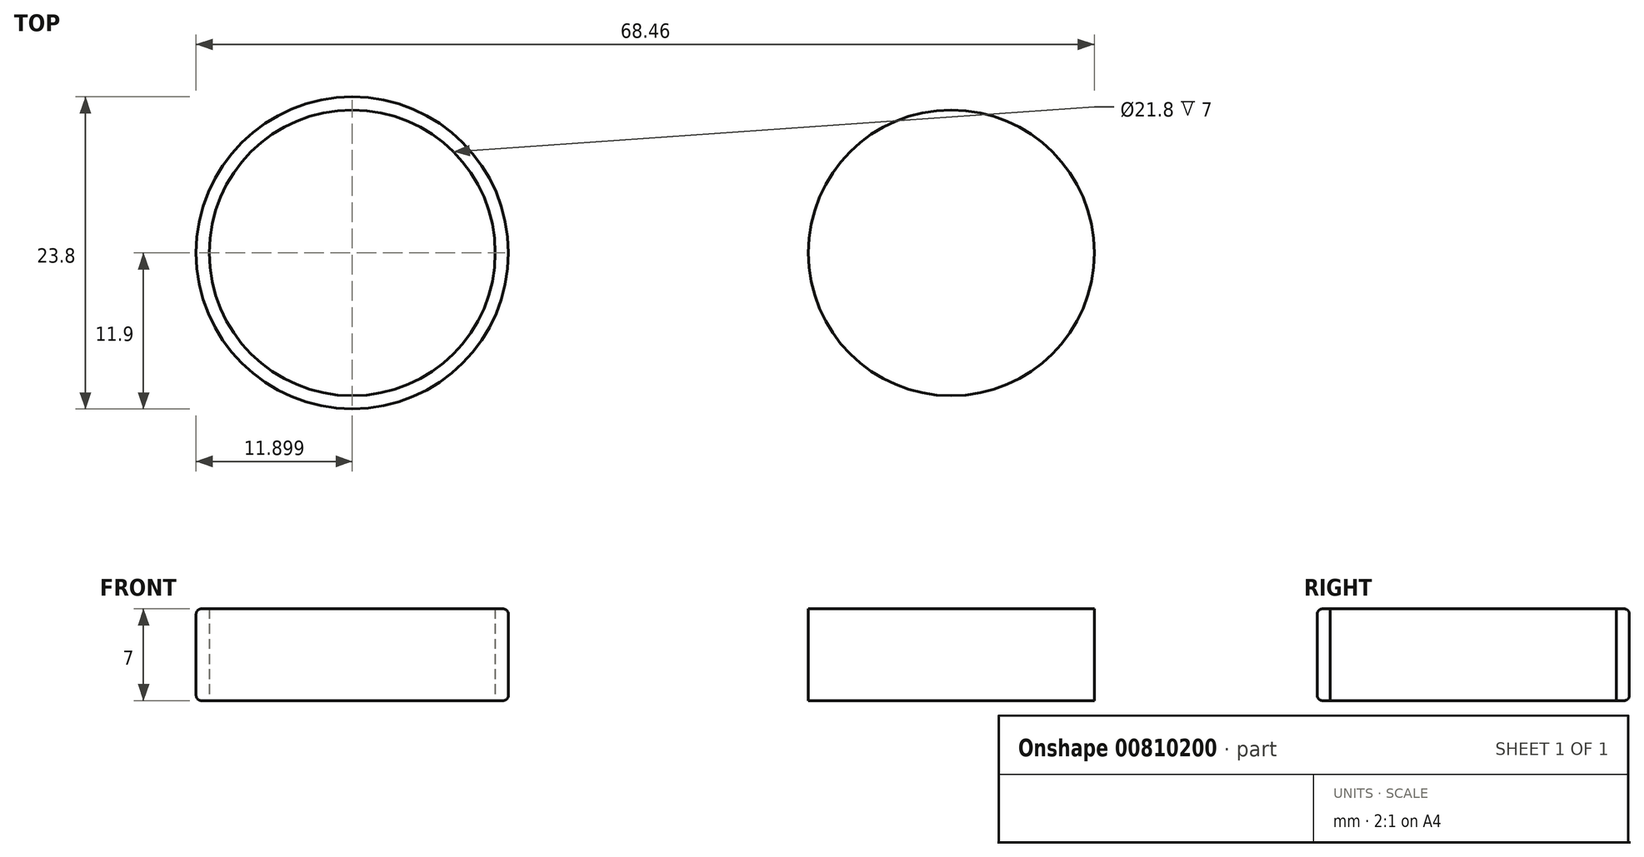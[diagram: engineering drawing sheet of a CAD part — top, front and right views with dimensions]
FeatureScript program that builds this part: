
annotation { "Feature Type Name" : "Feature", "Feature Type Description" : "" }
export const myFeature = defineFeature(function(context is Context, id is Id, definition is map)
    precondition{}
    {
        {
            var Q0;
            Q0=qCreatedBy(makeId("Top.planeOp"),FACE);
            var sketch = newSketch(context, id + "F0", { "sketchPlane" : qUnion([Q0])});
            skCircle(sketch, "E0", {"center": v(0, 0) * mm, "radius": 10.9 * mm});
            skCircle(sketch, "E1", {"center": v(0, 0) * mm, "radius": 11.9 * mm});
            skCircle(sketch, "E2", {"center": v(-22.83, 0) * mm, "radius": 10.9 * mm});
            skCircle(sketch, "E3", {"center": v(-22.83, 0) * mm, "radius": 11.9 * mm});
            skCircle(sketch, "E4.MirrorC", {"center": v(22.83, 0) * mm, "radius": 10.9 * mm});
            skCircle(sketch, "E5.MirrorC", {"center": v(22.83, 0) * mm, "radius": 11.9 * mm});
            skSolve(sketch);
        }
        {
            var Q0;
            {var subQ0=sQuery(id+"F0.wireOp",EDGE,"E1");var subQ1=sQuery(id+"F0.wireOp",EDGE,"E3");var subQ2=makeQuery(id+"F0.imprint","INTERSECT",VERTEX,{"disambiguationData":[OD(0.0)],"derivedFrom":[subQ1,subQ0]});Q0=makeQuery(id+"F0.imprint","IMPRINT",FACE,{"disambiguationData":[TD([[makeQuery(id+"F0.imprint","IMPRINT",EDGE,{"disambiguationData":[TD([[subQ2,1.0]])],"derivedFrom":subQ1}),1.0]])]});}
            var Q1;
            Q1=makeQuery(id+"F0.imprint","IMPRINT",FACE,{"disambiguationData":[TD([[makeQuery(id+"F0.imprint","IMPRINT",EDGE,{"derivedFrom":sQuery(id+"F0.wireOp",EDGE,"E0")}),1.0]])]});
            var Q2;
            Q2=makeQuery(id+"F0.imprint","IMPRINT",FACE,{"disambiguationData":[TD([[makeQuery(id+"F0.imprint","IMPRINT",EDGE,{"derivedFrom":sQuery(id+"F0.wireOp",EDGE,"E2")}),-1.0]])]});
            var Q3;
            {var subQ0=sQuery(id+"F0.wireOp",EDGE,"E5.MirrorC");var subQ1=sQuery(id+"F0.wireOp",EDGE,"E1");var subQ2=makeQuery(id+"F0.imprint","INTERSECT",VERTEX,{"disambiguationData":[OD(0.0)],"derivedFrom":[subQ1,subQ0]});Q3=makeQuery(id+"F0.imprint","IMPRINT",FACE,{"disambiguationData":[TD([[makeQuery(id+"F0.imprint","IMPRINT",EDGE,{"disambiguationData":[TD([[subQ2,-1.0]])],"derivedFrom":subQ1}),-1.0]])]});}
            var Q4;
            Q4=makeQuery(id+"F0.imprint","IMPRINT",FACE,{"disambiguationData":[TD([[makeQuery(id+"F0.imprint","IMPRINT",EDGE,{"derivedFrom":sQuery(id+"F0.wireOp",EDGE,"E4.MirrorC")}),1.0]])]});
            extrude(context, id + "F1", {"entities" : qUnion([Q0, Q1, Q2, Q3, Q4]), "depth" : 7 * mm, "offsetDistance" : 25 * mm});
        }
        {
            var Q0;
            Q0=makeQuery(id+"F1.opExtrude","CAP_EDGE",EDGE,{"disambiguationData":[OSD([sQuery(id+"F0.wireOp",EDGE,"E3")])],"isStart":false});
            var Q1;
            Q1=makeQuery(id+"F1.opExtrude","CAP_EDGE",EDGE,{"disambiguationData":[OSD([sQuery(id+"F0.wireOp",EDGE,"E5.MirrorC")])],"isStart":false});
            var Q2;
            Q2=makeQuery(id+"F1.opExtrude","CAP_EDGE",EDGE,{"disambiguationData":[OSD([sQuery(id+"F0.wireOp",EDGE,"E5.MirrorC")])],"isStart":true});
            var Q3;
            Q3=makeQuery(id+"F1.opExtrude","CAP_EDGE",EDGE,{"disambiguationData":[OSD([sQuery(id+"F0.wireOp",EDGE,"E3")])],"isStart":true});
            var Q4;
            {var subQ0=sQuery(id+"F0.wireOp",EDGE,"E1");Q4=makeQuery(id+"F1.opExtrude","CAP_EDGE",EDGE,{"disambiguationData":[OSD([subQ0]),TDD([makeQuery(id+"F0.imprint","IMPRINT",EDGE,{"disambiguationData":[TD([[makeQuery(id+"F0.imprint","INTERSECT",VERTEX,{"disambiguationData":[OD(1.0)],"derivedFrom":[sQuery(id+"F0.wireOp",EDGE,"E3"),subQ0]}),1.0]])],"derivedFrom":subQ0})])],"isStart":true});}
            var Q5;
            {var subQ0=sQuery(id+"F0.wireOp",EDGE,"E1");Q5=makeQuery(id+"F1.opExtrude","CAP_EDGE",EDGE,{"disambiguationData":[OSD([subQ0]),TDD([makeQuery(id+"F0.imprint","IMPRINT",EDGE,{"disambiguationData":[TD([[makeQuery(id+"F0.imprint","INTERSECT",VERTEX,{"disambiguationData":[OD(1.0)],"derivedFrom":[sQuery(id+"F0.wireOp",EDGE,"E3"),subQ0]}),1.0]])],"derivedFrom":subQ0})])],"isStart":false});}
            var Q6;
            {var subQ0=sQuery(id+"F0.wireOp",EDGE,"E1");Q6=makeQuery(id+"F1.opExtrude","CAP_EDGE",EDGE,{"disambiguationData":[OSD([subQ0]),TDD([makeQuery(id+"F0.imprint","IMPRINT",EDGE,{"disambiguationData":[TD([[makeQuery(id+"F0.imprint","INTERSECT",VERTEX,{"disambiguationData":[OD(0.0)],"derivedFrom":[sQuery(id+"F0.wireOp",EDGE,"E3"),subQ0]}),-1.0]])],"derivedFrom":subQ0})])],"isStart":false});}
            var Q7;
            {var subQ0=sQuery(id+"F0.wireOp",EDGE,"E1");Q7=makeQuery(id+"F1.opExtrude","CAP_EDGE",EDGE,{"disambiguationData":[OSD([subQ0]),TDD([makeQuery(id+"F0.imprint","IMPRINT",EDGE,{"disambiguationData":[TD([[makeQuery(id+"F0.imprint","INTERSECT",VERTEX,{"disambiguationData":[OD(0.0)],"derivedFrom":[sQuery(id+"F0.wireOp",EDGE,"E3"),subQ0]}),-1.0]])],"derivedFrom":subQ0})])],"isStart":true});}
            fillet(context, id + "F2", {"entities" : qUnion([Q0, Q1, Q2, Q3, Q4, Q5, Q6, Q7]), "radius" : 0.4 * mm, "tangentPropagation" : true, "allowEdgeOverflow" : false});
        }
    });
